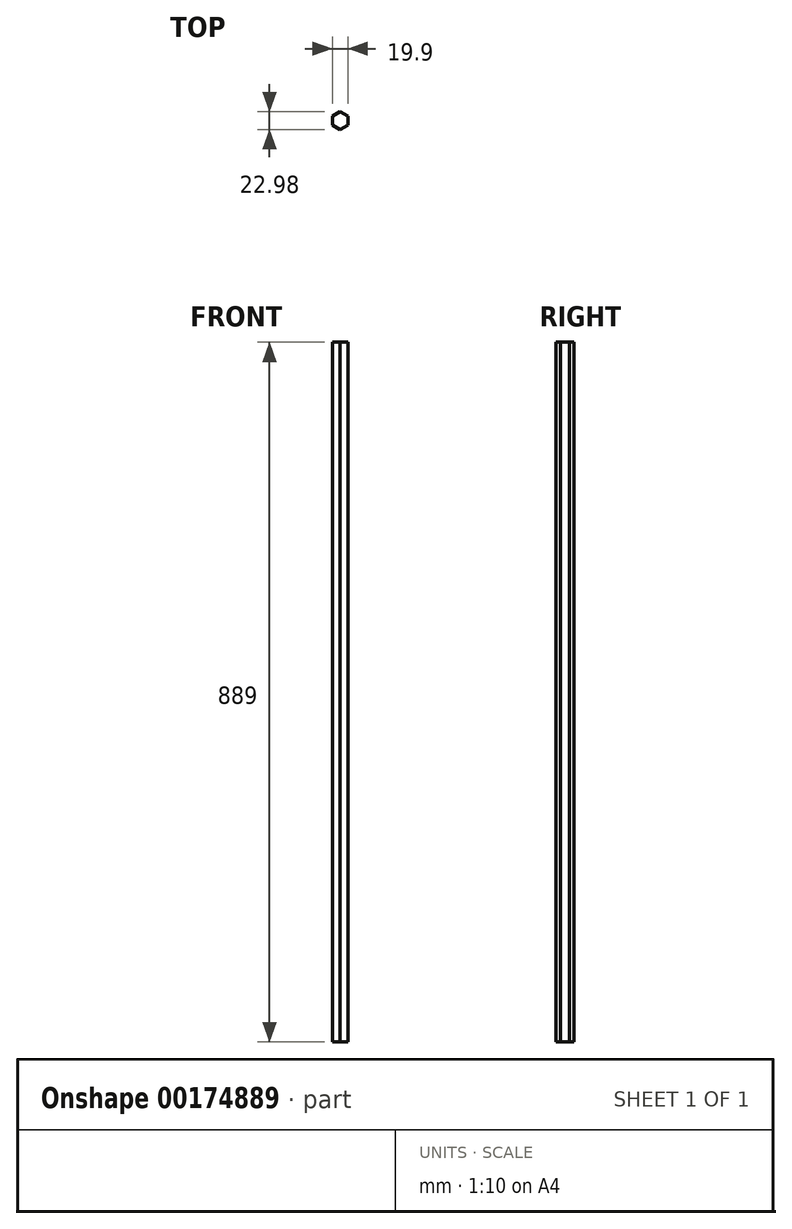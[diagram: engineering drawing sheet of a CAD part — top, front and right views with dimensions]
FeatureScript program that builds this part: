
annotation { "Feature Type Name" : "Feature", "Feature Type Description" : "" }
export const myFeature = defineFeature(function(context is Context, id is Id, definition is map)
    precondition{}
    {
        {
            var Q0;
            Q0=qCreatedBy(makeId("Top.planeOp"),FACE);
            var sketch = newSketch(context, id + "F0", { "sketchPlane" : qUnion([Q0])});
            skCircle(sketch, "E0.cCircle", {"center": v(0, 0) * mm, "radius": 9.95 * mm, "construction": true});
            skLineSegment(sketch, "E0.0", {"start": v(9.95, 5.74) * mm, "end": v(9.95, -5.74) * mm});
            skLineSegment(sketch, "E0.1", {"start": v(9.95, -5.74) * mm, "end": v(0, -11.49) * mm});
            skLineSegment(sketch, "E0.2", {"start": v(0, -11.49) * mm, "end": v(-9.95, -5.74) * mm});
            skLineSegment(sketch, "E0.3", {"start": v(-9.95, -5.74) * mm, "end": v(-9.95, 5.74) * mm});
            skLineSegment(sketch, "E0.4", {"start": v(-9.95, 5.74) * mm, "end": v(0, 11.49) * mm});
            skLineSegment(sketch, "E0.5", {"start": v(0, 11.49) * mm, "end": v(9.95, 5.74) * mm});
            skPoint(sketch, "E0.0.midPoint", {"position": v(9.95, 0) * mm});
            skSolve(sketch);
        }
        {
            var Q0;
            Q0=qSketchRegion(id+"F0",true);
            extrude(context, id + "F1", {"entities" : qUnion([Q0]), "depth" : 889 * mm});
        }
    });
